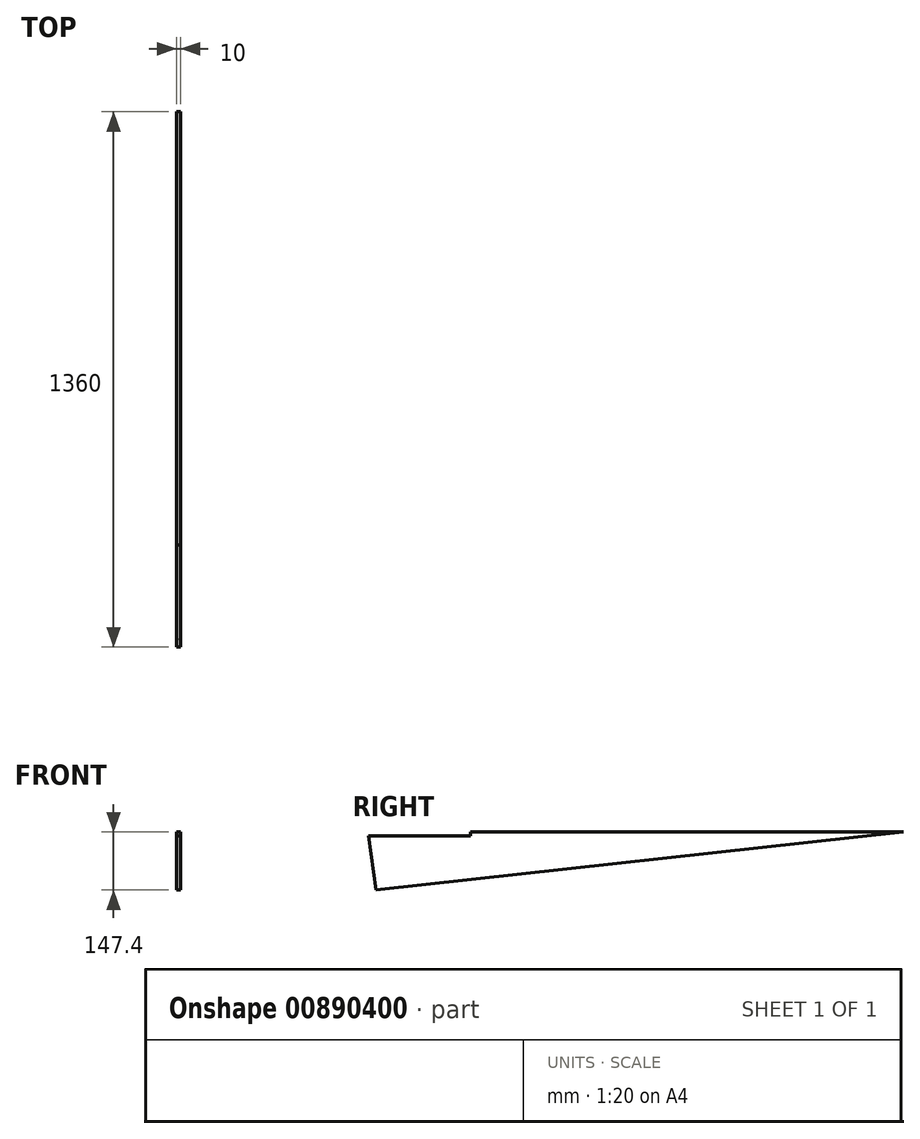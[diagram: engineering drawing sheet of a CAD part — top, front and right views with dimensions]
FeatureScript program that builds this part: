
annotation { "Feature Type Name" : "Feature", "Feature Type Description" : "" }
export const myFeature = defineFeature(function(context is Context, id is Id, definition is map)
    precondition{}
    {
        {
            var Q0;
            Q0=qCreatedBy(makeId("Right.planeOp"),FACE);
            var sketch = newSketch(context, id + "F0", { "sketchPlane" : qUnion([Q0])});
            skLineSegment(sketch, "E0", {"start": v(-338.57, 42.1) * mm, "end": v(-318.57, -95.3) * mm});
            skLineSegment(sketch, "E1", {"start": v(-318.57, -95.3) * mm, "end": v(1021.43, 52.1) * mm});
            skLineSegment(sketch, "E2", {"start": v(1021.43, 52.1) * mm, "end": v(-78.57, 52.1) * mm});
            skLineSegment(sketch, "E3", {"start": v(-78.57, 52.1) * mm, "end": v(-78.57, 42.1) * mm});
            skLineSegment(sketch, "E4", {"start": v(-78.57, 42.1) * mm, "end": v(-338.57, 42.1) * mm});
            skSolve(sketch);
        }
        {
            var Q0;
            Q0=makeQuery(id+"F0.imprint","IMPRINT",FACE,{"disambiguationData":[TD([[makeQuery(id+"F0.imprint","IMPRINT",EDGE,{"derivedFrom":sQuery(id+"F0.wireOp",EDGE,"E0")}),1.0]])]});
            extrude(context, id + "F1", {"entities" : qUnion([Q0]), "depth" : 10 * mm, "offsetDistance" : 25 * mm});
        }
    });
